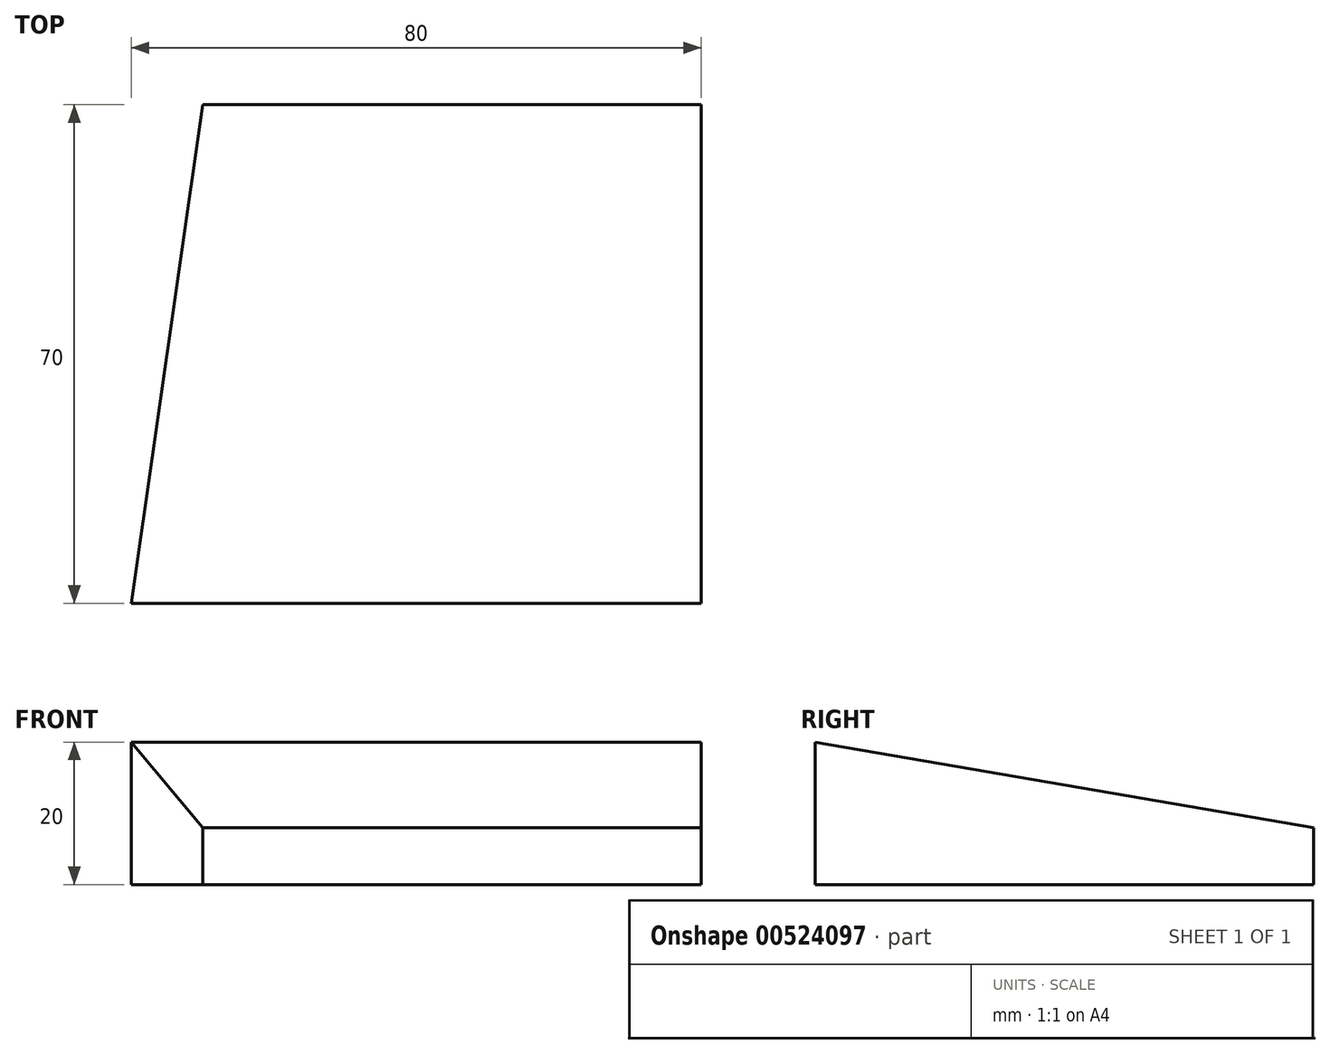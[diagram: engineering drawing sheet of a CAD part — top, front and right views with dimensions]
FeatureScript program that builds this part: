
annotation { "Feature Type Name" : "Feature", "Feature Type Description" : "" }
export const myFeature = defineFeature(function(context is Context, id is Id, definition is map)
    precondition{}
    {
        {
            var Q0;
            Q0=qCreatedBy(makeId("Front.planeOp"),FACE);
            var sketch = newSketch(context, id + "F0", { "sketchPlane" : qUnion([Q0])});
            skLineSegment(sketch, "E0", {"start": v(0, 0) * mm, "end": v(0, 20) * mm});
            skLineSegment(sketch, "E1", {"start": v(0, 20) * mm, "end": v(80, 20) * mm});
            skLineSegment(sketch, "E2", {"start": v(80, 20) * mm, "end": v(80, 0) * mm});
            skLineSegment(sketch, "E3", {"start": v(80, 0) * mm, "end": v(0, 0) * mm});
            skSolve(sketch);
        }
        {
            var Q0;
            Q0=qCreatedBy(makeId("Front.planeOp"),FACE);
            cPlane(context, id + "F1", {"entities" : qUnion([Q0]), "cplaneType" : CPlaneType.OFFSET, "offset" : 70 * mm, "oppositeDirection" : true, "width" : 150 * mm, "height" : 150 * mm});
        }
        {
            var Q0;
            Q0=qCreatedBy(id+"F1.planeOp",FACE);
            var sketch = newSketch(context, id + "F2", { "sketchPlane" : qUnion([Q0])});
            skLineSegment(sketch, "E4.bottom", {"start": v(10, 0) * mm, "end": v(80, 0) * mm});
            skLineSegment(sketch, "E4.top", {"start": v(10, 8) * mm, "end": v(80, 8) * mm});
            skLineSegment(sketch, "E4.left", {"start": v(10, 0) * mm, "end": v(10, 8) * mm});
            skLineSegment(sketch, "E4.right", {"start": v(80, 0) * mm, "end": v(80, 8) * mm});
            skSolve(sketch);
        }
        {
            var Q0;
            Q0=makeQuery(id+"F0.imprint","IMPRINT",FACE,{"disambiguationData":[TD([[makeQuery(id+"F0.imprint","IMPRINT",EDGE,{"derivedFrom":sQuery(id+"F0.wireOp",EDGE,"E0")}),-1.0]])]});
            var Q1;
            Q1=makeQuery(id+"F2.imprint","IMPRINT",FACE,{"disambiguationData":[TD([[makeQuery(id+"F2.imprint","IMPRINT",EDGE,{"derivedFrom":sQuery(id+"F2.wireOp",EDGE,"E4.bottom")}),1.0]])]});
            var Q2;
            Q2=makeQuery(id+"F0.imprint","IMPRINT",FACE,{"disambiguationData":[TD([[makeQuery(id+"F0.imprint","IMPRINT",EDGE,{"derivedFrom":sQuery(id+"F0.wireOp",EDGE,"E0")}),-1.0]])]});
            var Q3;
            Q3=makeQuery(id+"F2.imprint","IMPRINT",FACE,{"disambiguationData":[TD([[makeQuery(id+"F2.imprint","IMPRINT",EDGE,{"derivedFrom":sQuery(id+"F2.wireOp",EDGE,"E4.bottom")}),1.0]])]});
            loft(context, id + "F3", {"bodyType" : ToolBodyType.SURFACE, "sheetProfilesArray" : [{ "sheetProfileEntities" : qUnion([Q0]) }, { "sheetProfileEntities" : qUnion([Q1]) }], "wireProfilesArray" : [{ "wireProfileEntities" : qUnion([Q2]) }, { "wireProfileEntities" : qUnion([Q3]) }]});
        }
    });
